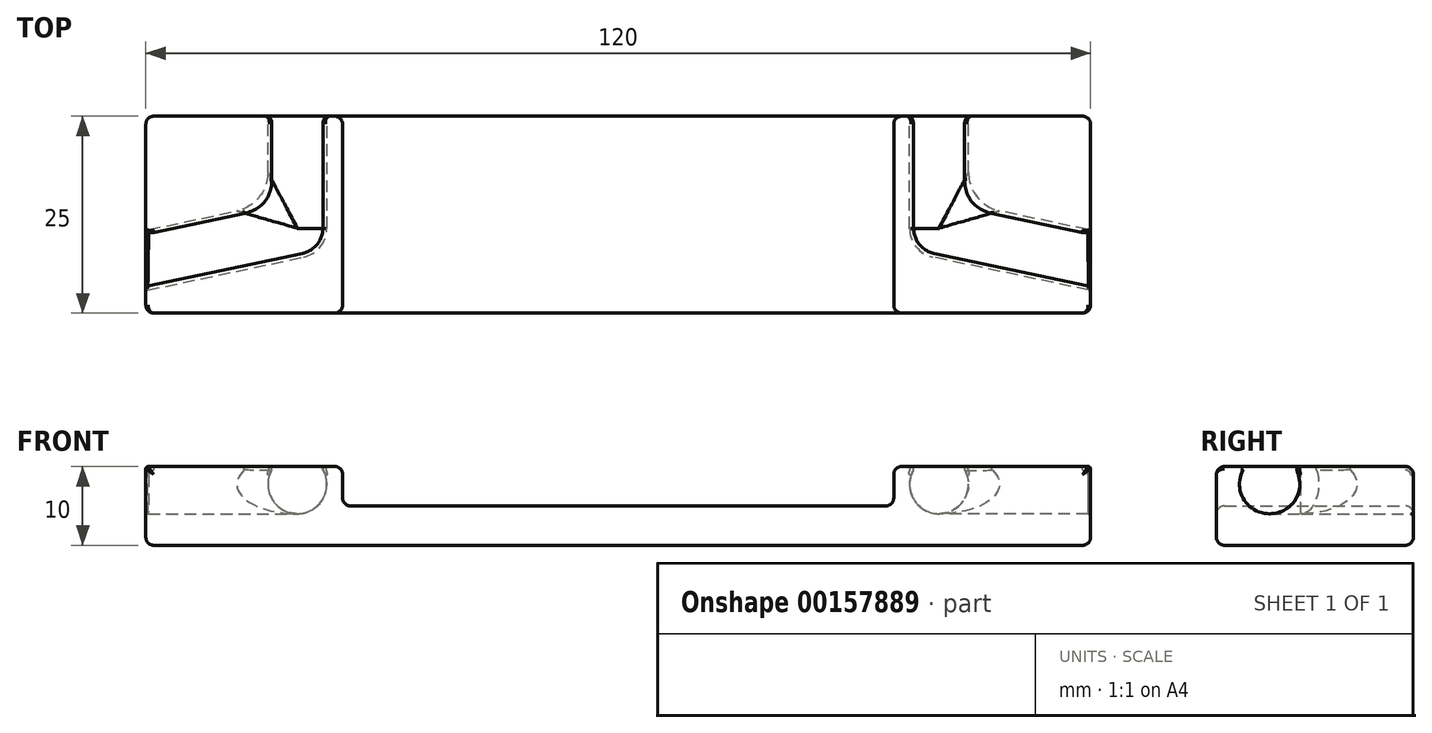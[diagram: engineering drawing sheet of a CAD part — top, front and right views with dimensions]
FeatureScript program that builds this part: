
annotation { "Feature Type Name" : "Feature", "Feature Type Description" : "" }
export const myFeature = defineFeature(function(context is Context, id is Id, definition is map)
    precondition{}
    {
        {
            var Q0;
            Q0=qCreatedBy(makeId("Front.planeOp"),FACE);
            var sketch = newSketch(context, id + "F0", { "sketchPlane" : qUnion([Q0])});
            skLineSegment(sketch, "E0.bottom", {"start": v(-35, 5) * mm, "end": v(-37.75, 5) * mm});
            skLineSegment(sketch, "E0.top", {"start": v(-35, -5) * mm, "end": v(-60, -5) * mm});
            skLineSegment(sketch, "E0.left", {"start": v(-35, 5) * mm, "end": v(-35, 0) * mm});
            skLineSegment(sketch, "E0.right", {"start": v(-60, 5) * mm, "end": v(-60, -5) * mm});
            skPoint(sketch, "E0.middle", {"position": v(-47.5, 0) * mm});
            skPoint(sketch, "E1.oppositeSnap0", {"position": v(-35, 0) * mm});
            skLineSegment(sketch, "E1.bottom", {"start": v(-35, -5) * mm, "end": v(0, -5) * mm});
            skLineSegment(sketch, "E1.top", {"start": v(-35, 0) * mm, "end": v(0, 0) * mm});
            skLineSegment(sketch, "E1.right", {"start": v(0, -5) * mm, "end": v(0, 0) * mm});
            skArc(sketch, "E2", {"start": v(-43.75, 5) * mm, "mid": v(-40.75, -1) * mm, "end": v(-37.75, 5) * mm});
            skLineSegment(sketch, "E3.trimOffspring", {"start": v(-43.75, 5) * mm, "end": v(-60, 5) * mm});
            skLineSegment(sketch, "E4", {"start": v(-43.75, 5) * mm, "end": v(-37.75, 5) * mm});
            skSolve(sketch);
        }
        {
            var Q0;
            Q0=makeQuery(id+"F0.imprint","IMPRINT",FACE,{"disambiguationData":[TD([[makeQuery(id+"F0.imprint","IMPRINT",EDGE,{"derivedFrom":sQuery(id+"F0.wireOp",EDGE,"E0.bottom")}),1.0]])]});
            var Q1;
            Q1=makeQuery(id+"F0.imprint","IMPRINT",FACE,{"disambiguationData":[TD([[makeQuery(id+"F0.imprint","IMPRINT",EDGE,{"derivedFrom":sQuery(id+"F0.wireOp",EDGE,"E2")}),1.0]])]});
            extrude(context, id + "F1", {"entities" : qUnion([Q0, Q1]), "depth" : 25 * mm});
        }
        {
            var Q0;
            Q0=makeQuery(id+"F0.imprint","IMPRINT",FACE,{"disambiguationData":[TD([[makeQuery(id+"F0.imprint","IMPRINT",EDGE,{"derivedFrom":sQuery(id+"F0.wireOp",EDGE,"E2")}),1.0]])]});
            extrude(context, id + "F2", {"entities" : qUnion([Q0]), "operationType" : NewBodyOperationType.REMOVE, "depth" : 14.25 * mm});
        }
        {
            var Q0;
            Q0=makeQuery(id+"F1.opExtrude","SWEPT_FACE",FACE,{"disambiguationData":[OSD([sQuery(id+"F0.wireOp",EDGE,"E3.trimOffspring")])]});
            var sketch = newSketch(context, id + "F3", { "sketchPlane" : qUnion([Q0])});
            skLineSegment(sketch, "E5", {"start": v(-35, 0) * mm, "end": v(-35, -13) * mm});
            skLineSegment(sketch, "E6", {"start": v(-35, -13) * mm, "end": v(-60.1, -18.33) * mm});
            skLineSegment(sketch, "E7", {"start": v(-60.1, -18.33) * mm, "end": v(-60.1, -25.34) * mm});
            skSolve(sketch);
        }
        {
            var Q0;
            Q0=sQuery(id+"F3.wireOp",EDGE,"E6");
            cPlane(context, id + "F4", {"entities" : qUnion([Q0]), "cplaneType" : CPlaneType.LINE_ANGLE, "offset" : 25 * mm, "angle" : 0 * degree, "width" : 150 * mm, "height" : 150 * mm});
        }
        {
            var Q0;
            Q0=qCreatedBy(id+"F4.planeOp",FACE);
            var sketch = newSketch(context, id + "F5", { "sketchPlane" : qUnion([Q0])});
            skLineSegment(sketch, "E8.0", {"start": v(-36.94, 5) * mm, "end": v(-62.6, 5) * mm});
            skLineSegment(sketch, "E9.right", {"start": v(-42.84, 6.5) * mm, "end": v(-42.84, -1) * mm});
            skLineSegment(sketch, "E10", {"start": v(-67.84, 2.75) * mm, "end": v(-42.84, 2.75) * mm});
            skLineSegment(sketch, "E11.bottom", {"start": v(-42.84, 6.5) * mm, "end": v(-67.84, 6.5) * mm});
            skLineSegment(sketch, "E11.top", {"start": v(-42.84, -1) * mm, "end": v(-67.84, -1) * mm});
            skLineSegment(sketch, "E11.right", {"start": v(-67.84, 6.5) * mm, "end": v(-67.84, -1) * mm});
            skArc(sketch, "E12", {"start": v(-42.84, -1) * mm, "mid": v(-39.09, 2.75) * mm, "end": v(-42.84, 6.5) * mm});
            skSolve(sketch);
        }
        {
            var Q0;
            {var subQ0=sQuery(id+"F5.wireOp",EDGE,"E12");var subQ1=sQuery(id+"F5.wireOp",EDGE,"E8.0");var subQ2=makeQuery(id+"F5.imprint","INTERSECT",VERTEX,{"derivedFrom":[subQ1,subQ0]});Q0=makeQuery(id+"F5.imprint","IMPRINT",FACE,{"disambiguationData":[TD([[makeQuery(id+"F5.imprint","IMPRINT",EDGE,{"disambiguationData":[TD([[subQ2,-1.0]])],"derivedFrom":subQ1}),-1.0]])]});}
            var Q1;
            {var subQ0=sQuery(id+"F5.wireOp",EDGE,"E12");var subQ1=sQuery(id+"F5.wireOp",EDGE,"E8.0");var subQ2=makeQuery(id+"F5.imprint","INTERSECT",VERTEX,{"derivedFrom":[subQ1,subQ0]});Q1=makeQuery(id+"F5.imprint","IMPRINT",FACE,{"disambiguationData":[TD([[makeQuery(id+"F5.imprint","IMPRINT",EDGE,{"disambiguationData":[TD([[subQ2,-1.0]])],"derivedFrom":subQ1}),1.0]])]});}
            var Q2;
            Q2=sQuery(id+"F5.wireOp",EDGE,"E9.right");
            revolve(context, id + "F6", {"operationType" : NewBodyOperationType.REMOVE, "entities" : qUnion([Q0, Q1]), "axis" : qUnion([Q2]), "revolveType" : RevolveType.FULL});
        }
        {
            var Q0;
            {var subQ3=sQuery(id+"F5.wireOp",EDGE,"E10");Q0=makeQuery(id+"F5.imprint","IMPRINT",FACE,{"disambiguationData":[TD([[makeQuery(id+"F5.imprint","IMPRINT",EDGE,{"derivedFrom":subQ3}),1.0]])]});}
            var Q1;
            Q1=sQuery(id+"F5.wireOp",EDGE,"E10");
            revolve(context, id + "F7", {"operationType" : NewBodyOperationType.REMOVE, "entities" : qUnion([Q0]), "axis" : qUnion([Q1]), "revolveType" : RevolveType.FULL, "oppositeDirection" : true});
        }
        {
            var Q0;
            Q0=makeQuery(id+"F7.boolean.opBoolean","INTERSECT",EDGE,{"derivedFrom":[makeQuery(id+"F2.boolean.opBoolean","COPY",FACE,{"derivedFrom":makeQuery(id+"F2.opExtrude","SWEPT_FACE",FACE,{"disambiguationData":[OSD([sQuery(id+"F0.wireOp",EDGE,"E2")])]})}),makeQuery(id+"F7.opRevolve","SWEPT_FACE",FACE,{"disambiguationData":[OSD([sQuery(id+"F5.wireOp",EDGE,"E11.bottom")])]})]});
            fillet(context, id + "F8", {"entities" : qUnion([Q0]), "radius" : 5 * mm, "tangentPropagation" : true, "allowEdgeOverflow" : false});
        }
        {
            var Q0;
            Q0=makeQuery(id+"F1.opExtrude","CAP_EDGE",EDGE,{"disambiguationData":[OSD([sQuery(id+"F0.wireOp",EDGE,"E1.top")])],"isStart":false});
            var Q1;
            Q1=makeQuery(id+"F1.opExtrude","SWEPT_EDGE",EDGE,{"disambiguationData":[OSD([sQuery(id+"F0.wireOp",EDGE,"E0.bottom"),sQuery(id+"F0.wireOp",EDGE,"E0.left")])]});
            var Q2;
            Q2=makeQuery(id+"F1.opExtrude","CAP_EDGE",EDGE,{"disambiguationData":[OSD([sQuery(id+"F0.wireOp",EDGE,"E0.bottom"),sQuery(id+"F0.wireOp",EDGE,"E3.trimOffspring"),sQuery(id+"F0.wireOp",EDGE,"E4")])],"isStart":false});
            var Q3;
            Q3=makeQuery(id+"F1.opExtrude","CAP_EDGE",EDGE,{"disambiguationData":[OSD([sQuery(id+"F0.wireOp",EDGE,"E0.right")])],"isStart":false});
            var Q4;
            Q4=makeQuery(id+"F1.opExtrude","CAP_EDGE",EDGE,{"disambiguationData":[OSD([sQuery(id+"F0.wireOp",EDGE,"E0.top"),sQuery(id+"F0.wireOp",EDGE,"E1.bottom")])],"isStart":false});
            var Q5;
            Q5=makeQuery(id+"F1.opExtrude","SWEPT_EDGE",EDGE,{"disambiguationData":[OSD([sQuery(id+"F0.wireOp",EDGE,"E0.top"),sQuery(id+"F0.wireOp",EDGE,"E0.right")])]});
            var Q6;
            {var subQ0=sQuery(id+"F0.wireOp",EDGE,"E4");var subQ1=sQuery(id+"F0.wireOp",EDGE,"E3.trimOffspring");var subQ2=sQuery(id+"F0.wireOp",EDGE,"E0.right");var subQ3=sQuery(id+"F0.wireOp",EDGE,"E0.bottom");Q6=makeQuery(id+"F7.boolean.opBoolean","SPLIT",EDGE,{"disambiguationData":[TD([makeQuery(id+"F1.opExtrude","CAP_FACE",FACE,{"disambiguationData":[OSD([subQ3,sQuery(id+"F0.wireOp",EDGE,"E0.top"),sQuery(id+"F0.wireOp",EDGE,"E0.left"),subQ2,sQuery(id+"F0.wireOp",EDGE,"E1.bottom"),sQuery(id+"F0.wireOp",EDGE,"E1.top"),sQuery(id+"F0.wireOp",EDGE,"E1.right"),subQ1,subQ0])],"isStart":true})])],"derivedFrom":makeQuery(id+"F1.opExtrude","SWEPT_EDGE",EDGE,{"disambiguationData":[OSD([subQ2,subQ1])]})});}
            var Q7;
            Q7=makeQuery(id+"F1.opExtrude","CAP_EDGE",EDGE,{"disambiguationData":[OSD([sQuery(id+"F0.wireOp",EDGE,"E0.left")])],"isStart":false});
            var Q8;
            Q8=makeQuery(id+"F1.opExtrude","SWEPT_EDGE",EDGE,{"disambiguationData":[OSD([sQuery(id+"F0.wireOp",EDGE,"E0.left"),sQuery(id+"F0.wireOp",EDGE,"E1.top")])]});
            fillet(context, id + "F9", {"entities" : qUnion([Q0, Q1, Q2, Q3, Q4, Q5, Q6, Q7, Q8]), "radius" : 1 * mm, "tangentPropagation" : true, "allowEdgeOverflow" : false});
        }
        {
            var Q0;
            {var subQ0=sQuery(id+"F0.wireOp",EDGE,"E4");var subQ1=sQuery(id+"F0.wireOp",EDGE,"E3.trimOffspring");var subQ2=sQuery(id+"F0.wireOp",EDGE,"E0.right");var subQ3=sQuery(id+"F0.wireOp",EDGE,"E0.bottom");Q0=makeQuery(id+"F2.boolean.opBoolean","SPLIT",EDGE,{"disambiguationData":[TD([makeQuery(id+"F1.opExtrude","SWEPT_FACE",FACE,{"disambiguationData":[OSD([subQ2])]})])],"derivedFrom":makeQuery(id+"F1.opExtrude","CAP_EDGE",EDGE,{"disambiguationData":[OSD([subQ3,subQ1,subQ0])],"isStart":true})});}
            var Q1;
            Q1=makeQuery(id+"F1.opExtrude","CAP_EDGE",EDGE,{"disambiguationData":[OSD([sQuery(id+"F0.wireOp",EDGE,"E1.top")])],"isStart":true});
            fillet(context, id + "F10", {"entities" : qUnion([Q0, Q1]), "radius" : 1 * mm, "tangentPropagation" : true, "allowEdgeOverflow" : false});
        }
        {
            var Q0;
            {var subQ0=sQuery(id+"F0.wireOp",EDGE,"E4");var subQ1=sQuery(id+"F0.wireOp",EDGE,"E3.trimOffspring");var subQ2=sQuery(id+"F0.wireOp",EDGE,"E0.right");var subQ3=sQuery(id+"F0.wireOp",EDGE,"E0.bottom");var subQ4=makeQuery(id+"F2.boolean.opBoolean","COPY",FACE,{"derivedFrom":makeQuery(id+"F2.opExtrude","SWEPT_FACE",FACE,{"disambiguationData":[OSD([sQuery(id+"F0.wireOp",EDGE,"E2")])]})});var subQ5=makeQuery(id+"F7.opRevolve","SWEPT_FACE",FACE,{"disambiguationData":[OSD([sQuery(id+"F5.wireOp",EDGE,"E11.bottom")])]});Q0=makeQuery(id+"F8.opFillet","BLEND_EDGE",EDGE,{"blendedFrom":[makeQuery(id+"F7.boolean.opBoolean","INTERSECT",EDGE,{"derivedFrom":[subQ4,subQ5]}),makeQuery(id+"F7.boolean.opBoolean","SPLIT",FACE,{"disambiguationData":[TD([makeQuery(id+"F1.opExtrude","CAP_FACE",FACE,{"disambiguationData":[OSD([subQ3,sQuery(id+"F0.wireOp",EDGE,"E0.top"),sQuery(id+"F0.wireOp",EDGE,"E0.left"),subQ2,sQuery(id+"F0.wireOp",EDGE,"E1.bottom"),sQuery(id+"F0.wireOp",EDGE,"E1.top"),sQuery(id+"F0.wireOp",EDGE,"E1.right"),subQ1,subQ0])],"isStart":true}),makeQuery(id+"F1.opExtrude","SWEPT_FACE",FACE,{"disambiguationData":[OSD([subQ2])]}),subQ4,subQ5])],"derivedFrom":makeQuery(id+"F1.opExtrude","SWEPT_FACE",FACE,{"disambiguationData":[OSD([subQ3,subQ1,subQ0])]})})],"blendedInto":[makeQuery(id+"F7.boolean.opBoolean","SPLIT",FACE,{"disambiguationData":[TD([makeQuery(id+"F1.opExtrude","CAP_FACE",FACE,{"disambiguationData":[OSD([subQ3,sQuery(id+"F0.wireOp",EDGE,"E0.top"),sQuery(id+"F0.wireOp",EDGE,"E0.left"),subQ2,sQuery(id+"F0.wireOp",EDGE,"E1.bottom"),sQuery(id+"F0.wireOp",EDGE,"E1.top"),sQuery(id+"F0.wireOp",EDGE,"E1.right"),subQ1,subQ0])],"isStart":true}),makeQuery(id+"F1.opExtrude","SWEPT_FACE",FACE,{"disambiguationData":[OSD([subQ2])]}),subQ4,subQ5])],"derivedFrom":makeQuery(id+"F1.opExtrude","SWEPT_FACE",FACE,{"disambiguationData":[OSD([subQ3,subQ1,subQ0])]})})]});}
            fillet(context, id + "F11", {"entities" : qUnion([Q0]), "radius" : 0.3 * mm, "tangentPropagation" : true, "allowEdgeOverflow" : false});
        }
        {
            var Q0;
            Q0=makeQuery(id+"F6.boolean.opBoolean","INTERSECT",EDGE,{"derivedFrom":[makeQuery(id+"F1.opExtrude","SWEPT_FACE",FACE,{"disambiguationData":[OSD([sQuery(id+"F0.wireOp",EDGE,"E0.bottom"),sQuery(id+"F0.wireOp",EDGE,"E3.trimOffspring"),sQuery(id+"F0.wireOp",EDGE,"E4")])]}),makeQuery(id+"F6.opRevolve","SWEPT_FACE",FACE,{"disambiguationData":[OSD([sQuery(id+"F5.wireOp",EDGE,"E12")])]})]});
            fillet(context, id + "F12", {"entities" : qUnion([Q0]), "radius" : 0.3 * mm, "tangentPropagation" : true, "allowEdgeOverflow" : false});
        }
        {
            var Q0;
            Q0=makeQuery(id+"F1.opExtrude","SWEPT_BODY",BODY,{"disambiguationData":[OSD([sQuery(id+"F0.wireOp",EDGE,"E0.bottom"),sQuery(id+"F0.wireOp",EDGE,"E0.top"),sQuery(id+"F0.wireOp",EDGE,"E0.left"),sQuery(id+"F0.wireOp",EDGE,"E0.right"),sQuery(id+"F0.wireOp",EDGE,"E1.bottom"),sQuery(id+"F0.wireOp",EDGE,"E1.top"),sQuery(id+"F0.wireOp",EDGE,"E1.right"),sQuery(id+"F0.wireOp",EDGE,"E3.trimOffspring"),sQuery(id+"F0.wireOp",EDGE,"E4")])]});
            var Q1;
            Q1=qCreatedBy(makeId("Right.planeOp"),FACE);
            mirror(context, id + "F13", {"operationType" : NewBodyOperationType.ADD, "entities" : qUnion([Q0]), "mirrorPlane" : qUnion([Q1])});
        }
    });
